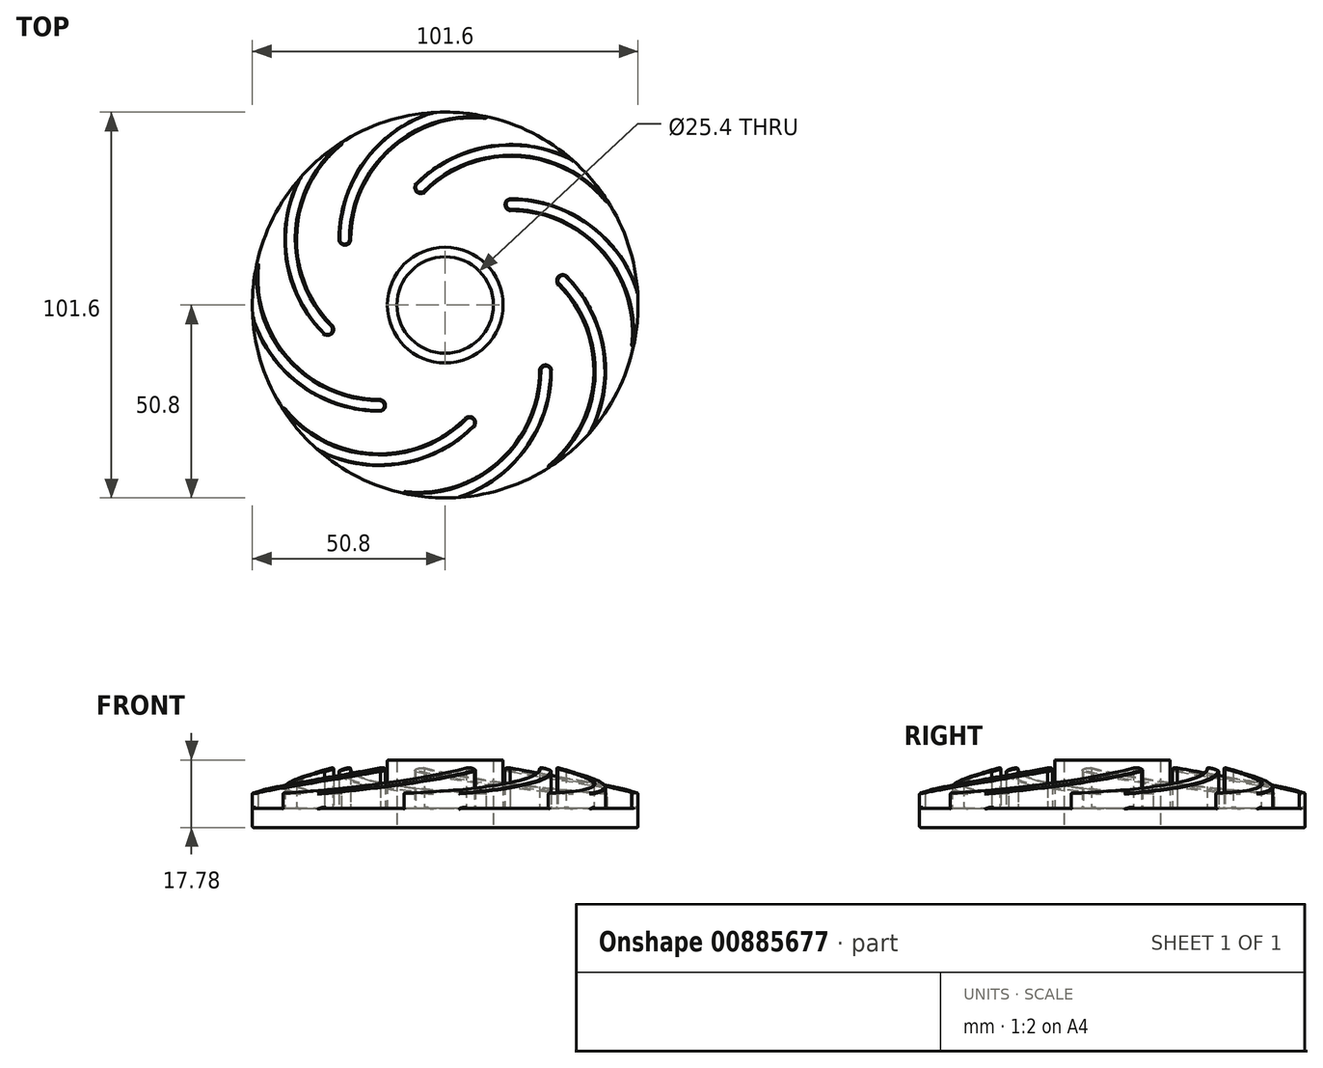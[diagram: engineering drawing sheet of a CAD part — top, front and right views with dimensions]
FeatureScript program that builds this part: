
annotation { "Feature Type Name" : "Feature", "Feature Type Description" : "" }
export const myFeature = defineFeature(function(context is Context, id is Id, definition is map)
    precondition{}
    {
        {
            var Q0;
            Q0=qCreatedBy(makeId("Top.planeOp"),FACE);
            var sketch = newSketch(context, id + "F0", { "sketchPlane" : qUnion([Q0])});
            skCircle(sketch, "E0", {"center": v(0, 0) * mm, "radius": 12.7 * mm});
            skCircle(sketch, "E1", {"center": v(0, 0) * mm, "radius": 50.8 * mm});
            skSolve(sketch);
        }
        {
            var Q0;
            Q0 = qSketchRegion(id + "F0", true);
            extrude(context, id + "F1", {"entities" : qUnion([Q0]), "depth" : 5.08 * mm, "offsetDistance" : 25.4 * mm});
        }
        {
            var Q0;
            Q0=makeQuery(id+"F1.opExtrude","CAP_FACE",FACE,{"disambiguationData":[OSD([sQuery(id+"F0.wireOp",EDGE,"E0"),sQuery(id+"F0.wireOp",EDGE,"E1")])],"isStart":false});
            var sketch = newSketch(context, id + "F2", { "sketchPlane" : qUnion([Q0])});
            skCircle(sketch, "E2", {"center": v(0, 0) * mm, "radius": 12.7 * mm});
            skCircle(sketch, "E3", {"center": v(0, 0) * mm, "radius": 15.24 * mm});
            skSolve(sketch);
        }
        {
            var Q0;
            Q0 = qSketchRegion(id + "F2", true);
            extrude(context, id + "F3", {"entities" : qUnion([Q0]), "operationType" : NewBodyOperationType.ADD, "depth" : 12.7 * mm, "offsetDistance" : 25.4 * mm});
        }
        {
            var Q0;
            Q0=makeQuery(id+"F1.opExtrude","CAP_FACE",FACE,{"disambiguationData":[OSD([sQuery(id+"F0.wireOp",EDGE,"E0"),sQuery(id+"F0.wireOp",EDGE,"E1")])],"isStart":false});
            var Q1;
            Q1=makeQuery(id+"F1.opExtrude","CAP_FACE",FACE,{"disambiguationData":[OSD([sQuery(id+"F0.wireOp",EDGE,"E0"),sQuery(id+"F0.wireOp",EDGE,"E1")])],"isStart":false});
            var Q2;
            Q2=makeQuery(id+"F1.opExtrude","CAP_FACE",FACE,{"disambiguationData":[OSD([sQuery(id+"F0.wireOp",EDGE,"E0"),sQuery(id+"F0.wireOp",EDGE,"E1")])],"isStart":false});
            var Q3;
            Q3=makeQuery(id+"F1.opExtrude","CAP_FACE",FACE,{"disambiguationData":[OSD([sQuery(id+"F0.wireOp",EDGE,"E0"),sQuery(id+"F0.wireOp",EDGE,"E1")])],"isStart":false});
            var sketch = newSketch(context, id + "F4", { "sketchPlane" : qUnion([Q0, Q1, Q2, Q3])});
            skArc(sketch, "E4.0.0", {"start": v(-46.84, 19.67) * mm, "mid": v(-50.14, 8.19) * mm, "end": v(-50.66, -3.75) * mm});
            skArc(sketch, "E5.0.0", {"start": v(-19.2, 47.03) * mm, "mid": v(-29.66, 41.24) * mm, "end": v(-38.47, 33.17) * mm});
            skArc(sketch, "E6", {"start": v(46.84, -19.67) * mm, "mid": v(43.93, 10.62) * mm, "end": v(17.05, 24.89) * mm});
            skArc(sketch, "E7", {"start": v(17.05, 27.97) * mm, "mid": v(15.77, 26.43) * mm, "end": v(17.05, 24.89) * mm});
            skArc(sketch, "E8", {"start": v(50.66, 3.75) * mm, "mid": v(37.8, 21.32) * mm, "end": v(17.05, 27.97) * mm});
            skArc(sketch, "E9.1.0", {"start": v(33.17, 38.47) * mm, "mid": v(11.65, 41.8) * mm, "end": v(-7.72, 31.83) * mm});
            skArc(sketch, "E9.1.1", {"start": v(47.03, 19.2) * mm, "mid": v(23.55, 38.57) * mm, "end": v(-5.54, 29.66) * mm});
            skArc(sketch, "E9.1.2", {"start": v(-7.72, 31.83) * mm, "mid": v(-7.54, 29.83) * mm, "end": v(-5.54, 29.66) * mm});
            skArc(sketch, "E9.2.0", {"start": v(-3.75, 50.66) * mm, "mid": v(-21.32, 37.8) * mm, "end": v(-27.97, 17.05) * mm});
            skArc(sketch, "E9.2.1", {"start": v(19.67, 46.84) * mm, "mid": v(-10.62, 43.93) * mm, "end": v(-24.89, 17.05) * mm});
            skArc(sketch, "E9.2.2", {"start": v(-27.97, 17.05) * mm, "mid": v(-26.43, 15.77) * mm, "end": v(-24.89, 17.05) * mm});
            skArc(sketch, "E9.3.0", {"start": v(-38.47, 33.17) * mm, "mid": v(-41.8, 11.65) * mm, "end": v(-31.83, -7.72) * mm});
            skArc(sketch, "E9.3.1", {"start": v(-19.2, 47.03) * mm, "mid": v(-38.57, 23.55) * mm, "end": v(-29.66, -5.54) * mm});
            skArc(sketch, "E9.3.2", {"start": v(-31.83, -7.72) * mm, "mid": v(-29.83, -7.54) * mm, "end": v(-29.66, -5.54) * mm});
            skArc(sketch, "E9.4.0", {"start": v(-50.66, -3.75) * mm, "mid": v(-37.8, -21.32) * mm, "end": v(-17.05, -27.97) * mm});
            skArc(sketch, "E9.4.1", {"start": v(-46.84, 19.67) * mm, "mid": v(-43.93, -10.62) * mm, "end": v(-17.05, -24.89) * mm});
            skArc(sketch, "E9.4.2", {"start": v(-17.05, -27.97) * mm, "mid": v(-15.77, -26.43) * mm, "end": v(-17.05, -24.89) * mm});
            skArc(sketch, "E9.5.0", {"start": v(-33.17, -38.47) * mm, "mid": v(-11.65, -41.8) * mm, "end": v(7.72, -31.83) * mm});
            skArc(sketch, "E9.5.1", {"start": v(-47.03, -19.2) * mm, "mid": v(-23.55, -38.57) * mm, "end": v(5.54, -29.66) * mm});
            skArc(sketch, "E9.5.2", {"start": v(7.72, -31.83) * mm, "mid": v(7.54, -29.83) * mm, "end": v(5.54, -29.66) * mm});
            skArc(sketch, "E9.6.0", {"start": v(3.75, -50.66) * mm, "mid": v(21.32, -37.8) * mm, "end": v(27.97, -17.05) * mm});
            skArc(sketch, "E9.6.1", {"start": v(-19.67, -46.84) * mm, "mid": v(10.62, -43.93) * mm, "end": v(24.89, -17.05) * mm});
            skArc(sketch, "E9.6.2", {"start": v(27.97, -17.05) * mm, "mid": v(26.43, -15.77) * mm, "end": v(24.89, -17.05) * mm});
            skArc(sketch, "E9.7.0", {"start": v(38.47, -33.17) * mm, "mid": v(41.8, -11.65) * mm, "end": v(31.83, 7.72) * mm});
            skArc(sketch, "E9.7.1", {"start": v(19.2, -47.03) * mm, "mid": v(38.57, -23.55) * mm, "end": v(29.66, 5.54) * mm});
            skArc(sketch, "E9.7.2", {"start": v(31.83, 7.72) * mm, "mid": v(29.83, 7.54) * mm, "end": v(29.66, 5.54) * mm});
            skArc(sketch, "E10.trimOffspring", {"start": v(19.67, 46.84) * mm, "mid": v(8.19, 50.14) * mm, "end": v(-3.75, 50.66) * mm});
            skArc(sketch, "E11.trimOffspring", {"start": v(47.03, 19.2) * mm, "mid": v(41.24, 29.66) * mm, "end": v(33.17, 38.47) * mm});
            skArc(sketch, "E12.trimOffspring", {"start": v(46.84, -19.67) * mm, "mid": v(50.14, -8.19) * mm, "end": v(50.66, 3.75) * mm});
            skArc(sketch, "E13.trimOffspring", {"start": v(19.2, -47.03) * mm, "mid": v(29.66, -41.24) * mm, "end": v(38.47, -33.17) * mm});
            skArc(sketch, "E14.trimOffspring", {"start": v(-19.67, -46.84) * mm, "mid": v(-8.19, -50.14) * mm, "end": v(3.75, -50.66) * mm});
            skArc(sketch, "E15.trimOffspring", {"start": v(-47.03, -19.2) * mm, "mid": v(-41.24, -29.66) * mm, "end": v(-33.17, -38.47) * mm});
            skSolve(sketch);
        }
        {
            var Q0;
            Q0 = qSketchRegion(id + "F4", true);
            extrude(context, id + "F5", {"entities" : qUnion([Q0]), "operationType" : NewBodyOperationType.ADD, "depth" : 12.7 * mm, "offsetDistance" : 25.4 * mm});
        }
        {
            var Q0;
            Q0=qCreatedBy(makeId("Front.planeOp"),FACE);
            var sketch = newSketch(context, id + "F6", { "sketchPlane" : qUnion([Q0])});
            skLineSegment(sketch, "E16", {"start": v(24.4, 17.65) * mm, "end": v(62.98, 4.98) * mm});
            skPoint(sketch, "E16.endSnap0", {"position": v(12.2, 4.98) * mm});
            skLineSegment(sketch, "E17", {"start": v(62.98, 4.98) * mm, "end": v(62.98, 22.01) * mm});
            skLineSegment(sketch, "E18", {"start": v(62.98, 22.01) * mm, "end": v(18.5, 22.01) * mm});
            skLineSegment(sketch, "E19", {"start": v(18.5, 22.01) * mm, "end": v(24.4, 17.65) * mm});
            skPoint(sketch, "E20.trimOffspring.end.orphan", {"position": v(0, -7.7) * mm});
            skPoint(sketch, "E21.0.start.orphan", {"position": v(-15.24, 17.78) * mm});
            skSolve(sketch);
        }
        {
            var Q0;
            Q0=makeQuery(id+"F6.imprint","IMPRINT",FACE,{"disambiguationData":[TD([[makeQuery(id+"F6.imprint","IMPRINT",EDGE,{"derivedFrom":sQuery(id+"F6.wireOp",EDGE,"E16")}),1.0]])]});
            var Q1;
            Q1=makeQuery(id+"F3.opExtrude","CAP_EDGE",EDGE,{"disambiguationData":[OSD([sQuery(id+"F2.wireOp",EDGE,"E2")])],"isStart":false});
            revolve(context, id + "F7", {"operationType" : NewBodyOperationType.REMOVE, "surfaceOperationType" : NewSurfaceOperationType.NEW, "entities" : qUnion([Q0]), "axis" : qUnion([Q1]), "revolveType" : RevolveType.FULL, "oppositeDirection" : true});
        }
        {
            var Q0;
            {var subQ0=sQuery(id+"F0.wireOp",EDGE,"E1");Q0=makeQuery(id+"F5.boolean.opBoolean","SPLIT",EDGE,{"disambiguationData":[TD([makeQuery(id+"F5.opExtrude","SWEPT_FACE",FACE,{"disambiguationData":[OSD([sQuery(id+"F4.wireOp",EDGE,"E9.3.0")])]})])],"derivedFrom":makeQuery(id+"F1.opExtrude","CAP_EDGE",EDGE,{"disambiguationData":[OSD([subQ0])],"isStart":false})});}
            var Q1;
            Q1=makeQuery(id+"F5.opExtrude","SWEPT_EDGE",EDGE,{"disambiguationData":[OSD([sQuery(id+"F0.wireOp",EDGE,"E1"),sQuery(id+"F4.wireOp",EDGE,"E9.4.1"),sQuery(id+"F4.wireOp",EDGE,"E4.0.0")])]});
            var Q2;
            Q2=makeQuery(id+"F5.opExtrude","SWEPT_EDGE",EDGE,{"disambiguationData":[OSD([sQuery(id+"F0.wireOp",EDGE,"E1"),sQuery(id+"F4.wireOp",EDGE,"E9.5.1"),sQuery(id+"F4.wireOp",EDGE,"E15.trimOffspring")])]});
            var Q3;
            Q3=makeQuery(id+"F5.opExtrude","SWEPT_EDGE",EDGE,{"disambiguationData":[OSD([sQuery(id+"F0.wireOp",EDGE,"E1"),sQuery(id+"F4.wireOp",EDGE,"E9.6.1"),sQuery(id+"F4.wireOp",EDGE,"E14.trimOffspring")])]});
            var Q4;
            Q4=makeQuery(id+"F5.opExtrude","SWEPT_EDGE",EDGE,{"disambiguationData":[OSD([sQuery(id+"F0.wireOp",EDGE,"E1"),sQuery(id+"F4.wireOp",EDGE,"E9.7.1"),sQuery(id+"F4.wireOp",EDGE,"E13.trimOffspring")])]});
            var Q5;
            Q5=makeQuery(id+"F5.opExtrude","SWEPT_EDGE",EDGE,{"disambiguationData":[OSD([sQuery(id+"F0.wireOp",EDGE,"E1"),sQuery(id+"F4.wireOp",EDGE,"E9.3.1"),sQuery(id+"F4.wireOp",EDGE,"E5.0.0")])]});
            var Q6;
            Q6=makeQuery(id+"F5.opExtrude","SWEPT_EDGE",EDGE,{"disambiguationData":[OSD([sQuery(id+"F0.wireOp",EDGE,"E1"),sQuery(id+"F4.wireOp",EDGE,"E9.2.1"),sQuery(id+"F4.wireOp",EDGE,"E10.trimOffspring")])]});
            var Q7;
            Q7=makeQuery(id+"F5.opExtrude","SWEPT_EDGE",EDGE,{"disambiguationData":[OSD([sQuery(id+"F0.wireOp",EDGE,"E1"),sQuery(id+"F4.wireOp",EDGE,"E6"),sQuery(id+"F4.wireOp",EDGE,"E12.trimOffspring")])]});
            var Q8;
            Q8=makeQuery(id+"F5.opExtrude","SWEPT_EDGE",EDGE,{"disambiguationData":[OSD([sQuery(id+"F0.wireOp",EDGE,"E1"),sQuery(id+"F4.wireOp",EDGE,"E9.1.1"),sQuery(id+"F4.wireOp",EDGE,"E11.trimOffspring")])]});
            var Q9;
            Q9=makeQuery(id+"F5.opExtrude","SWEPT_EDGE",EDGE,{"disambiguationData":[OSD([sQuery(id+"F0.wireOp",EDGE,"E1"),sQuery(id+"F4.wireOp",EDGE,"E9.6.0"),sQuery(id+"F4.wireOp",EDGE,"E14.trimOffspring")])]});
            var Q10;
            {var subQ0=sQuery(id+"F0.wireOp",EDGE,"E1");Q10=makeQuery(id+"F5.boolean.opBoolean","SPLIT",EDGE,{"disambiguationData":[TD([makeQuery(id+"F5.opExtrude","SWEPT_FACE",FACE,{"disambiguationData":[OSD([sQuery(id+"F4.wireOp",EDGE,"E9.2.0")])]})])],"derivedFrom":makeQuery(id+"F1.opExtrude","CAP_EDGE",EDGE,{"disambiguationData":[OSD([subQ0])],"isStart":false})});}
            var Q11;
            {var subQ0=sQuery(id+"F0.wireOp",EDGE,"E1");Q11=makeQuery(id+"F5.boolean.opBoolean","SPLIT",EDGE,{"disambiguationData":[TD([makeQuery(id+"F5.opExtrude","SWEPT_FACE",FACE,{"disambiguationData":[OSD([sQuery(id+"F4.wireOp",EDGE,"E9.1.0")])]})])],"derivedFrom":makeQuery(id+"F1.opExtrude","CAP_EDGE",EDGE,{"disambiguationData":[OSD([subQ0])],"isStart":false})});}
            var Q12;
            {var subQ0=sQuery(id+"F0.wireOp",EDGE,"E1");Q12=makeQuery(id+"F5.boolean.opBoolean","SPLIT",EDGE,{"disambiguationData":[TD([makeQuery(id+"F5.opExtrude","SWEPT_FACE",FACE,{"disambiguationData":[OSD([sQuery(id+"F4.wireOp",EDGE,"E8")])]})])],"derivedFrom":makeQuery(id+"F1.opExtrude","CAP_EDGE",EDGE,{"disambiguationData":[OSD([subQ0])],"isStart":false})});}
            var Q13;
            {var subQ0=sQuery(id+"F0.wireOp",EDGE,"E1");Q13=makeQuery(id+"F5.boolean.opBoolean","SPLIT",EDGE,{"disambiguationData":[TD([makeQuery(id+"F5.opExtrude","SWEPT_FACE",FACE,{"disambiguationData":[OSD([sQuery(id+"F4.wireOp",EDGE,"E6")])]})])],"derivedFrom":makeQuery(id+"F1.opExtrude","CAP_EDGE",EDGE,{"disambiguationData":[OSD([subQ0])],"isStart":false})});}
            var Q14;
            {var subQ0=sQuery(id+"F0.wireOp",EDGE,"E1");Q14=makeQuery(id+"F5.boolean.opBoolean","SPLIT",EDGE,{"disambiguationData":[TD([makeQuery(id+"F5.opExtrude","SWEPT_FACE",FACE,{"disambiguationData":[OSD([sQuery(id+"F4.wireOp",EDGE,"E9.4.0")])]})])],"derivedFrom":makeQuery(id+"F1.opExtrude","CAP_EDGE",EDGE,{"disambiguationData":[OSD([subQ0])],"isStart":false})});}
            var Q15;
            {var subQ0=sQuery(id+"F0.wireOp",EDGE,"E1");Q15=makeQuery(id+"F5.boolean.opBoolean","SPLIT",EDGE,{"disambiguationData":[TD([makeQuery(id+"F5.opExtrude","SWEPT_FACE",FACE,{"disambiguationData":[OSD([sQuery(id+"F4.wireOp",EDGE,"E9.5.0")])]})])],"derivedFrom":makeQuery(id+"F1.opExtrude","CAP_EDGE",EDGE,{"disambiguationData":[OSD([subQ0])],"isStart":false})});}
            var Q16;
            {var subQ0=sQuery(id+"F0.wireOp",EDGE,"E1");Q16=makeQuery(id+"F5.boolean.opBoolean","SPLIT",EDGE,{"disambiguationData":[TD([makeQuery(id+"F5.opExtrude","SWEPT_FACE",FACE,{"disambiguationData":[OSD([sQuery(id+"F4.wireOp",EDGE,"E9.6.0")])]})])],"derivedFrom":makeQuery(id+"F1.opExtrude","CAP_EDGE",EDGE,{"disambiguationData":[OSD([subQ0])],"isStart":false})});}
            fillet(context, id + "F8", {"entities" : qUnion([Q0, Q1, Q2, Q3, Q4, Q5, Q6, Q7, Q8, Q9, Q10, Q11, Q12, Q13, Q14, Q15, Q16]), "radius" : 0.25 * mm, "tangentPropagation" : true, "allowEdgeOverflow" : false});
        }
        {
            var Q0;
            Q0=makeQuery(id+"F5.opExtrude","SWEPT_EDGE",EDGE,{"disambiguationData":[OSD([sQuery(id+"F0.wireOp",EDGE,"E1"),sQuery(id+"F4.wireOp",EDGE,"E9.5.0"),sQuery(id+"F4.wireOp",EDGE,"E15.trimOffspring")])]});
            var Q1;
            Q1=makeQuery(id+"F5.opExtrude","SWEPT_EDGE",EDGE,{"disambiguationData":[OSD([sQuery(id+"F0.wireOp",EDGE,"E1"),sQuery(id+"F4.wireOp",EDGE,"E9.4.0"),sQuery(id+"F4.wireOp",EDGE,"E4.0.0")])]});
            var Q2;
            Q2=makeQuery(id+"F5.opExtrude","SWEPT_EDGE",EDGE,{"disambiguationData":[OSD([sQuery(id+"F0.wireOp",EDGE,"E1"),sQuery(id+"F4.wireOp",EDGE,"E9.3.0"),sQuery(id+"F4.wireOp",EDGE,"E5.0.0")])]});
            var Q3;
            Q3=makeQuery(id+"F5.opExtrude","SWEPT_EDGE",EDGE,{"disambiguationData":[OSD([sQuery(id+"F0.wireOp",EDGE,"E1"),sQuery(id+"F4.wireOp",EDGE,"E9.7.0"),sQuery(id+"F4.wireOp",EDGE,"E13.trimOffspring")])]});
            var Q4;
            Q4=makeQuery(id+"F5.opExtrude","SWEPT_EDGE",EDGE,{"disambiguationData":[OSD([sQuery(id+"F0.wireOp",EDGE,"E1"),sQuery(id+"F4.wireOp",EDGE,"E8"),sQuery(id+"F4.wireOp",EDGE,"E12.trimOffspring")])]});
            var Q5;
            Q5=makeQuery(id+"F5.opExtrude","SWEPT_EDGE",EDGE,{"disambiguationData":[OSD([sQuery(id+"F0.wireOp",EDGE,"E1"),sQuery(id+"F4.wireOp",EDGE,"E9.1.0"),sQuery(id+"F4.wireOp",EDGE,"E11.trimOffspring")])]});
            var Q6;
            Q6=makeQuery(id+"F5.opExtrude","SWEPT_EDGE",EDGE,{"disambiguationData":[OSD([sQuery(id+"F0.wireOp",EDGE,"E1"),sQuery(id+"F4.wireOp",EDGE,"E9.2.0"),sQuery(id+"F4.wireOp",EDGE,"E10.trimOffspring")])]});
            var Q7;
            {var subQ0=sQuery(id+"F4.wireOp",EDGE,"E14.trimOffspring");var subQ1=sQuery(id+"F0.wireOp",EDGE,"E1");Q7=makeQuery(id+"F8.opFillet","BLEND_EDGE",EDGE,{"blendedFrom":[makeQuery(id+"F5.opExtrude","SWEPT_EDGE",EDGE,{"disambiguationData":[OSD([subQ1,sQuery(id+"F4.wireOp",EDGE,"E9.6.0"),subQ0])]}),makeQuery(id+"F5.boolean.opBoolean","MERGE",FACE,{"derivedFrom":[makeQuery(id+"F1.opExtrude","SWEPT_FACE",FACE,{"disambiguationData":[OSD([subQ1])]}),makeQuery(id+"F5.opExtrude","SWEPT_FACE",FACE,{"disambiguationData":[OSD([sQuery(id+"F4.wireOp",EDGE,"E10.trimOffspring")])]}),makeQuery(id+"F5.opExtrude","SWEPT_FACE",FACE,{"disambiguationData":[OSD([sQuery(id+"F4.wireOp",EDGE,"E4.0.0")])]}),makeQuery(id+"F5.opExtrude","SWEPT_FACE",FACE,{"disambiguationData":[OSD([sQuery(id+"F4.wireOp",EDGE,"E5.0.0")])]}),makeQuery(id+"F5.opExtrude","SWEPT_FACE",FACE,{"disambiguationData":[OSD([sQuery(id+"F4.wireOp",EDGE,"E11.trimOffspring")])]}),makeQuery(id+"F5.opExtrude","SWEPT_FACE",FACE,{"disambiguationData":[OSD([sQuery(id+"F4.wireOp",EDGE,"E12.trimOffspring")])]}),makeQuery(id+"F5.opExtrude","SWEPT_FACE",FACE,{"disambiguationData":[OSD([sQuery(id+"F4.wireOp",EDGE,"E13.trimOffspring")])]}),makeQuery(id+"F5.opExtrude","SWEPT_FACE",FACE,{"disambiguationData":[OSD([subQ0])]}),makeQuery(id+"F5.opExtrude","SWEPT_FACE",FACE,{"disambiguationData":[OSD([sQuery(id+"F4.wireOp",EDGE,"E15.trimOffspring")])]})]})],"blendedInto":[makeQuery(id+"F5.boolean.opBoolean","MERGE",FACE,{"derivedFrom":[makeQuery(id+"F1.opExtrude","SWEPT_FACE",FACE,{"disambiguationData":[OSD([subQ1])]}),makeQuery(id+"F5.opExtrude","SWEPT_FACE",FACE,{"disambiguationData":[OSD([sQuery(id+"F4.wireOp",EDGE,"E10.trimOffspring")])]}),makeQuery(id+"F5.opExtrude","SWEPT_FACE",FACE,{"disambiguationData":[OSD([sQuery(id+"F4.wireOp",EDGE,"E4.0.0")])]}),makeQuery(id+"F5.opExtrude","SWEPT_FACE",FACE,{"disambiguationData":[OSD([sQuery(id+"F4.wireOp",EDGE,"E5.0.0")])]}),makeQuery(id+"F5.opExtrude","SWEPT_FACE",FACE,{"disambiguationData":[OSD([sQuery(id+"F4.wireOp",EDGE,"E11.trimOffspring")])]}),makeQuery(id+"F5.opExtrude","SWEPT_FACE",FACE,{"disambiguationData":[OSD([sQuery(id+"F4.wireOp",EDGE,"E12.trimOffspring")])]}),makeQuery(id+"F5.opExtrude","SWEPT_FACE",FACE,{"disambiguationData":[OSD([sQuery(id+"F4.wireOp",EDGE,"E13.trimOffspring")])]}),makeQuery(id+"F5.opExtrude","SWEPT_FACE",FACE,{"disambiguationData":[OSD([subQ0])]}),makeQuery(id+"F5.opExtrude","SWEPT_FACE",FACE,{"disambiguationData":[OSD([sQuery(id+"F4.wireOp",EDGE,"E15.trimOffspring")])]})]})]});}
            var Q8;
            {var subQ0=sQuery(id+"F4.wireOp",EDGE,"E9.6.0");Q8=makeQuery(id+"F8.opFillet","BLEND_EDGE",EDGE,{"blendedFrom":[makeQuery(id+"F5.opExtrude","SWEPT_EDGE",EDGE,{"disambiguationData":[OSD([sQuery(id+"F0.wireOp",EDGE,"E1"),subQ0,sQuery(id+"F4.wireOp",EDGE,"E14.trimOffspring")])]}),makeQuery(id+"F5.opExtrude","SWEPT_FACE",FACE,{"disambiguationData":[OSD([subQ0])]})],"blendedInto":[makeQuery(id+"F5.opExtrude","SWEPT_FACE",FACE,{"disambiguationData":[OSD([subQ0])]})]});}
            fillet(context, id + "F9", {"entities" : qUnion([Q0, Q1, Q2, Q3, Q4, Q5, Q6, Q7, Q8]), "radius" : 5.08 * mm, "tangentPropagation" : true, "allowEdgeOverflow" : false});
        }
        {
            var Q0;
            Q0=makeQuery(id+"F3.opExtrude","SWEPT_FACE",FACE,{"disambiguationData":[OSD([sQuery(id+"F2.wireOp",EDGE,"E3")])]});
            var Q1;
            Q1=makeQuery(id+"F3.boolean.opBoolean","MERGE",FACE,{"derivedFrom":[makeQuery(id+"F1.opExtrude","SWEPT_FACE",FACE,{"disambiguationData":[OSD([sQuery(id+"F0.wireOp",EDGE,"E0")])]}),makeQuery(id+"F3.opExtrude","SWEPT_FACE",FACE,{"disambiguationData":[OSD([sQuery(id+"F2.wireOp",EDGE,"E2")])]})]});
            var Q2;
            Q2=makeQuery(id+"F1.opExtrude","CAP_FACE",FACE,{"disambiguationData":[OSD([sQuery(id+"F0.wireOp",EDGE,"E0"),sQuery(id+"F0.wireOp",EDGE,"E1")])],"isStart":true});
            var Q3;
            Q3=makeQuery(id+"F7.boolean.opBoolean","COPY",FACE,{"disambiguationData":[TD([makeQuery(id+"F5.opExtrude","SWEPT_FACE",FACE,{"disambiguationData":[OSD([sQuery(id+"F4.wireOp",EDGE,"E9.7.0")])]})])],"derivedFrom":makeQuery(id+"F7.opRevolve","SWEPT_FACE",FACE,{"disambiguationData":[OSD([sQuery(id+"F6.wireOp",EDGE,"E16")])]})});
            var Q4;
            Q4=makeQuery(id+"F7.boolean.opBoolean","COPY",FACE,{"disambiguationData":[TD([makeQuery(id+"F5.opExtrude","SWEPT_FACE",FACE,{"disambiguationData":[OSD([sQuery(id+"F4.wireOp",EDGE,"E6")])]})])],"derivedFrom":makeQuery(id+"F7.opRevolve","SWEPT_FACE",FACE,{"disambiguationData":[OSD([sQuery(id+"F6.wireOp",EDGE,"E16")])]})});
            var Q5;
            Q5=makeQuery(id+"F7.boolean.opBoolean","COPY",FACE,{"disambiguationData":[TD([makeQuery(id+"F5.opExtrude","SWEPT_FACE",FACE,{"disambiguationData":[OSD([sQuery(id+"F4.wireOp",EDGE,"E9.6.0")])]})])],"derivedFrom":makeQuery(id+"F7.opRevolve","SWEPT_FACE",FACE,{"disambiguationData":[OSD([sQuery(id+"F6.wireOp",EDGE,"E16")])]})});
            var Q6;
            Q6=makeQuery(id+"F7.boolean.opBoolean","COPY",FACE,{"disambiguationData":[TD([makeQuery(id+"F5.opExtrude","SWEPT_FACE",FACE,{"disambiguationData":[OSD([sQuery(id+"F4.wireOp",EDGE,"E9.5.0")])]})])],"derivedFrom":makeQuery(id+"F7.opRevolve","SWEPT_FACE",FACE,{"disambiguationData":[OSD([sQuery(id+"F6.wireOp",EDGE,"E16")])]})});
            var Q7;
            Q7=makeQuery(id+"F7.boolean.opBoolean","COPY",FACE,{"disambiguationData":[TD([makeQuery(id+"F5.opExtrude","SWEPT_FACE",FACE,{"disambiguationData":[OSD([sQuery(id+"F4.wireOp",EDGE,"E9.1.0")])]})])],"derivedFrom":makeQuery(id+"F7.opRevolve","SWEPT_FACE",FACE,{"disambiguationData":[OSD([sQuery(id+"F6.wireOp",EDGE,"E16")])]})});
            var Q8;
            Q8=makeQuery(id+"F7.boolean.opBoolean","COPY",FACE,{"disambiguationData":[TD([makeQuery(id+"F5.opExtrude","SWEPT_FACE",FACE,{"disambiguationData":[OSD([sQuery(id+"F4.wireOp",EDGE,"E9.2.0")])]})])],"derivedFrom":makeQuery(id+"F7.opRevolve","SWEPT_FACE",FACE,{"disambiguationData":[OSD([sQuery(id+"F6.wireOp",EDGE,"E16")])]})});
            var Q9;
            Q9=makeQuery(id+"F7.boolean.opBoolean","COPY",FACE,{"disambiguationData":[TD([makeQuery(id+"F5.opExtrude","SWEPT_FACE",FACE,{"disambiguationData":[OSD([sQuery(id+"F4.wireOp",EDGE,"E9.4.0")])]})])],"derivedFrom":makeQuery(id+"F7.opRevolve","SWEPT_FACE",FACE,{"disambiguationData":[OSD([sQuery(id+"F6.wireOp",EDGE,"E16")])]})});
            var Q10;
            Q10=makeQuery(id+"F7.boolean.opBoolean","COPY",FACE,{"disambiguationData":[TD([makeQuery(id+"F5.opExtrude","SWEPT_FACE",FACE,{"disambiguationData":[OSD([sQuery(id+"F4.wireOp",EDGE,"E9.3.0")])]})])],"derivedFrom":makeQuery(id+"F7.opRevolve","SWEPT_FACE",FACE,{"disambiguationData":[OSD([sQuery(id+"F6.wireOp",EDGE,"E16")])]})});
            fillet(context, id + "F10", {"entities" : qUnion([Q0, Q1, Q2, Q3, Q4, Q5, Q6, Q7, Q8, Q9, Q10]), "radius" : 0.25 * mm, "tangentPropagation" : true, "allowEdgeOverflow" : false});
        }
        {
            var Q0;
            Q0=makeQuery(id+"F1.opExtrude","CAP_FACE",FACE,{"disambiguationData":[OSD([sQuery(id+"F0.wireOp",EDGE,"E0"),sQuery(id+"F0.wireOp",EDGE,"E1")])],"isStart":false});
            fillet(context, id + "F11", {"entities" : qUnion([Q0]), "radius" : 0.25 * mm, "tangentPropagation" : true, "allowEdgeOverflow" : false});
        }
    });
